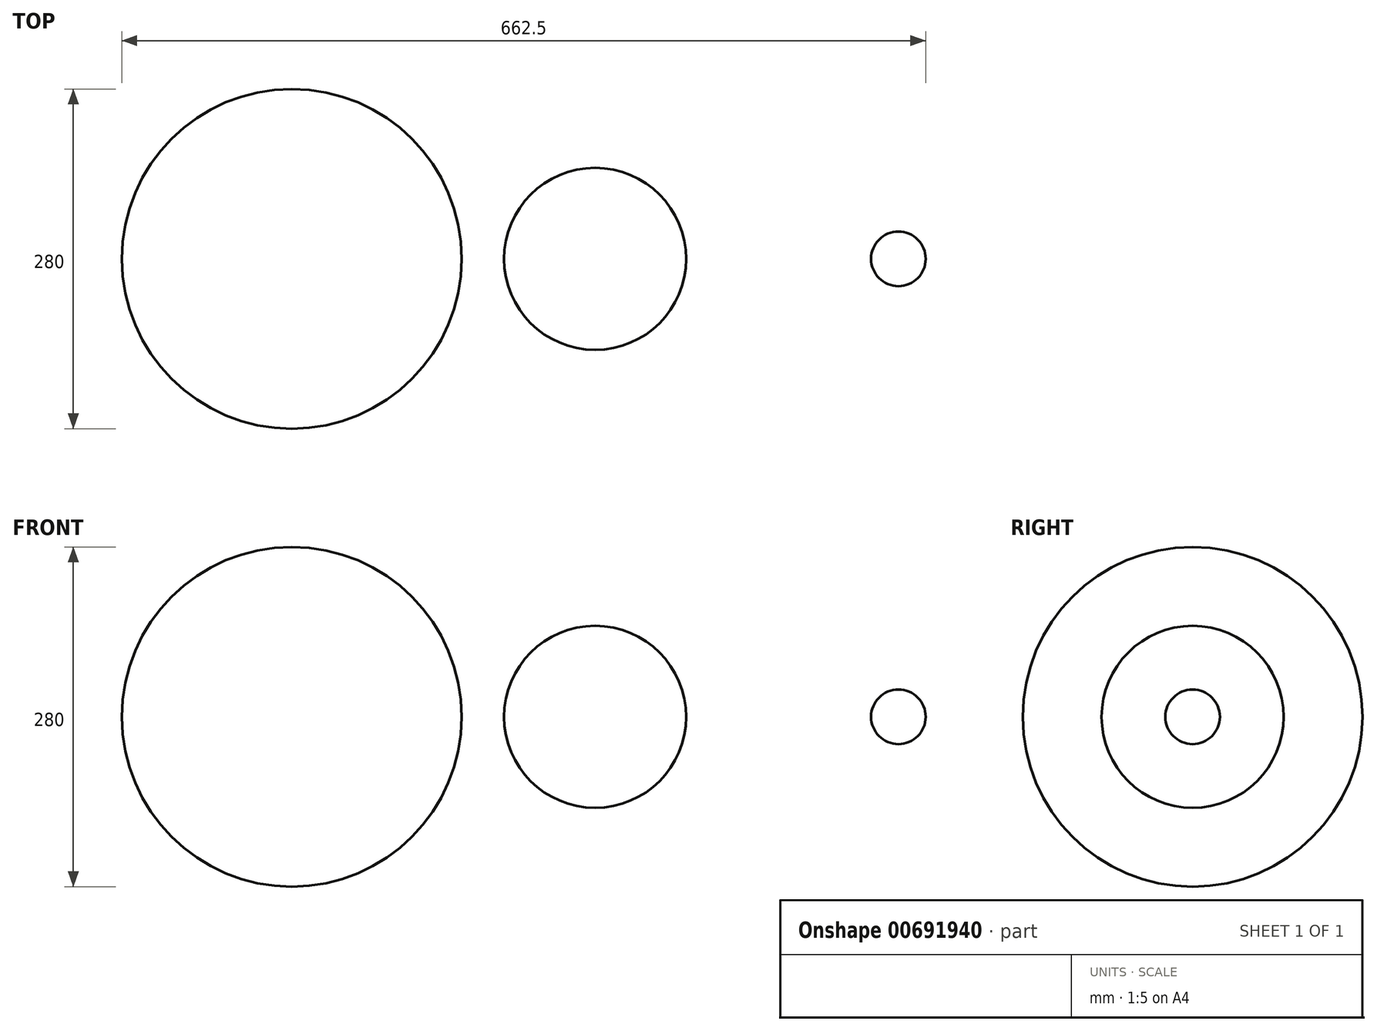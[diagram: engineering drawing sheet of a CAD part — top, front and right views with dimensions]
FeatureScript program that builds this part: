
annotation { "Feature Type Name" : "Feature", "Feature Type Description" : "" }
export const myFeature = defineFeature(function(context is Context, id is Id, definition is map)
    precondition{}
    {
        {
            var Q0;
            Q0=qCreatedBy(makeId("Front.planeOp"),FACE);
            var sketch = newSketch(context, id + "F0", { "sketchPlane" : qUnion([Q0])});
            skArc(sketch, "E0", {"start": v(0, -140) * mm, "mid": v(140, 0) * mm, "end": v(0, 140) * mm});
            skArc(sketch, "E1", {"start": v(250, -75) * mm, "mid": v(325, 0) * mm, "end": v(250, 75) * mm});
            skArc(sketch, "E2", {"start": v(500, -22.5) * mm, "mid": v(522.5, 0) * mm, "end": v(500, 22.5) * mm});
            skLineSegment(sketch, "E3", {"start": v(0, 140) * mm, "end": v(0, -140) * mm});
            skLineSegment(sketch, "E4", {"start": v(250, 75) * mm, "end": v(250, -75) * mm});
            skLineSegment(sketch, "E5", {"start": v(500, 22.5) * mm, "end": v(500, -22.5) * mm});
            skSolve(sketch);
        }
        {
            var Q0;
            Q0=makeQuery(id+"F0.imprint","IMPRINT",FACE,{"disambiguationData":[TD([[makeQuery(id+"F0.imprint","IMPRINT",EDGE,{"derivedFrom":sQuery(id+"F0.wireOp",EDGE,"E0")}),1.0]])]});
            var Q1;
            Q1=sQuery(id+"F0.wireOp",EDGE,"E3");
            revolve(context, id + "F1", {"entities" : qUnion([Q0]), "axis" : qUnion([Q1]), "revolveType" : RevolveType.FULL});
        }
        {
            var Q0;
            Q0=makeQuery(id+"F0.imprint","IMPRINT",FACE,{"disambiguationData":[TD([[makeQuery(id+"F0.imprint","IMPRINT",EDGE,{"derivedFrom":sQuery(id+"F0.wireOp",EDGE,"E1")}),1.0]])]});
            var Q1;
            Q1=sQuery(id+"F0.wireOp",EDGE,"E4");
            revolve(context, id + "F2", {"entities" : qUnion([Q0]), "axis" : qUnion([Q1]), "revolveType" : RevolveType.FULL});
        }
        {
            var Q0;
            Q0=makeQuery(id+"F0.imprint","IMPRINT",FACE,{"disambiguationData":[TD([[makeQuery(id+"F0.imprint","IMPRINT",EDGE,{"derivedFrom":sQuery(id+"F0.wireOp",EDGE,"E2")}),1.0]])]});
            var Q1;
            Q1=sQuery(id+"F0.wireOp",EDGE,"E5");
            revolve(context, id + "F3", {"entities" : qUnion([Q0]), "axis" : qUnion([Q1]), "revolveType" : RevolveType.FULL});
        }
    });
